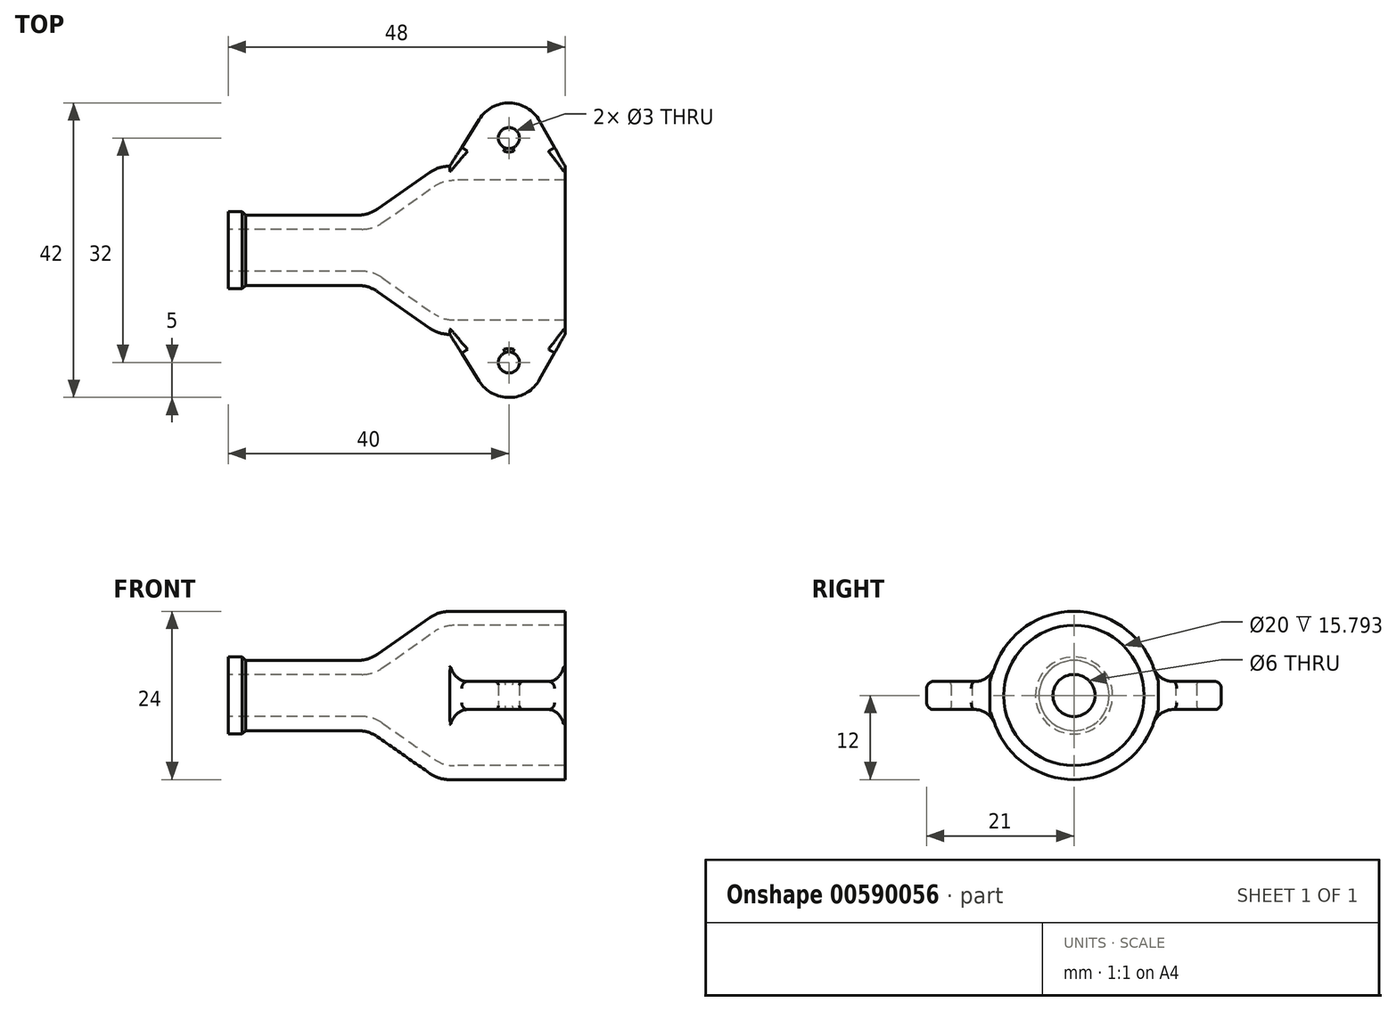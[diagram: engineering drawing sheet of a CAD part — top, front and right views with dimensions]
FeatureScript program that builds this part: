
annotation { "Feature Type Name" : "Feature", "Feature Type Description" : "" }
export const myFeature = defineFeature(function(context is Context, id is Id, definition is map)
    precondition{}
    {
        {
            var Q0;
            Q0=qCreatedBy(makeId("Front.planeOp"),FACE);
            var sketch = newSketch(context, id + "F0", { "sketchPlane" : qUnion([Q0])});
            skLineSegment(sketch, "E0", {"start": v(-50.98, 0) * mm, "end": v(49.02, 0) * mm, "construction": true});
            skLineSegment(sketch, "E1", {"start": v(-41.63, 5) * mm, "end": v(-23.63, 5) * mm});
            skLineSegment(sketch, "E2", {"start": v(-23.63, 5) * mm, "end": v(-13.63, 12) * mm});
            skLineSegment(sketch, "E3", {"start": v(-13.63, 12) * mm, "end": v(4.37, 12) * mm});
            skLineSegment(sketch, "E4", {"start": v(-43.63, 5) * mm, "end": v(-43.63, 3) * mm});
            skLineSegment(sketch, "E5", {"start": v(-43.63, 3) * mm, "end": v(-23, 3) * mm});
            skLineSegment(sketch, "E6", {"start": v(-23, 3) * mm, "end": v(-13, 10) * mm});
            skLineSegment(sketch, "E7", {"start": v(-13, 10) * mm, "end": v(4.37, 10) * mm});
            skLineSegment(sketch, "E8", {"start": v(4.37, 12) * mm, "end": v(4.37, 10) * mm});
            skLineSegment(sketch, "E9", {"start": v(-43.63, 5) * mm, "end": v(-43.63, 5.5) * mm});
            skLineSegment(sketch, "E10", {"start": v(-43.63, 5.5) * mm, "end": v(-41.63, 5.5) * mm});
            skLineSegment(sketch, "E11", {"start": v(-41.63, 5.5) * mm, "end": v(-41.63, 5) * mm});
            skSolve(sketch);
        }
        {
            var Q0;
            Q0 = qSketchRegion(id + "F0", true);
            var Q1;
            Q1=sQuery(id+"F0.wireOp",EDGE,"E0");
            revolve(context, id + "F1", {"entities" : qUnion([Q0]), "axis" : qUnion([Q1]), "revolveType" : RevolveType.FULL});
        }
        {
            var Q0;
            Q0=makeQuery(id+"F1.opRevolve","SWEPT_FACE",FACE,{"disambiguationData":[OSD([sQuery(id+"F0.wireOp",EDGE,"E8")])]});
            var sketch = newSketch(context, id + "F2", { "sketchPlane" : qUnion([Q0])});
            skLineSegment(sketch, "E12.bottom", {"start": v(-0.5, 25) * mm, "end": v(0.5, 25) * mm});
            skLineSegment(sketch, "E12.top", {"start": v(-0.5, -25) * mm, "end": v(0.5, -25) * mm});
            skLineSegment(sketch, "E12.left", {"start": v(-0.5, 25) * mm, "end": v(-0.5, 0.5) * mm});
            skLineSegment(sketch, "E12.right", {"start": v(0.5, 25) * mm, "end": v(0.5, 0.5) * mm});
            skLineSegment(sketch, "E13.bottom", {"start": v(-25, 0.5) * mm, "end": v(-0.5, 0.5) * mm});
            skLineSegment(sketch, "E13.top", {"start": v(-25, -0.5) * mm, "end": v(-0.5, -0.5) * mm});
            skLineSegment(sketch, "E13.left", {"start": v(-25, 0.5) * mm, "end": v(-25, -0.5) * mm});
            skLineSegment(sketch, "E13.right", {"start": v(25, 0.5) * mm, "end": v(25, -0.5) * mm});
            skLineSegment(sketch, "E14.trimOffspring", {"start": v(0.5, -0.5) * mm, "end": v(25, -0.5) * mm});
            skLineSegment(sketch, "E15.trimOffspring", {"start": v(0.5, 0.5) * mm, "end": v(25, 0.5) * mm});
            skLineSegment(sketch, "E16.trimOffspring", {"start": v(0.5, -0.5) * mm, "end": v(0.5, -25) * mm});
            skLineSegment(sketch, "E17.trimOffspring", {"start": v(-0.5, -0.5) * mm, "end": v(-0.5, -25) * mm});
            skSolve(sketch);
        }
        {
            var Q0;
            Q0=makeQuery(id+"F1.opRevolve","SWEPT_EDGE",EDGE,{"disambiguationData":[OSD([sQuery(id+"F0.wireOp",EDGE,"E1"),sQuery(id+"F0.wireOp",EDGE,"E2")])]});
            fillet(context, id + "F3", {"entities" : qUnion([Q0]), "radius" : 5 * mm, "tangentPropagation" : true, "allowEdgeOverflow" : false});
        }
        {
            var Q0;
            Q0=makeQuery(id+"F1.opRevolve","SWEPT_EDGE",EDGE,{"disambiguationData":[OSD([sQuery(id+"F0.wireOp",EDGE,"E2"),sQuery(id+"F0.wireOp",EDGE,"E3")])]});
            fillet(context, id + "F4", {"entities" : qUnion([Q0]), "radius" : 5 * mm, "tangentPropagation" : true, "allowEdgeOverflow" : false});
        }
        {
            var Q0;
            Q0=makeQuery(id+"F1.opRevolve","SWEPT_EDGE",EDGE,{"disambiguationData":[OSD([sQuery(id+"F0.wireOp",EDGE,"E6"),sQuery(id+"F0.wireOp",EDGE,"E7")])]});
            var Q1;
            Q1=makeQuery(id+"F1.opRevolve","SWEPT_EDGE",EDGE,{"disambiguationData":[OSD([sQuery(id+"F0.wireOp",EDGE,"E5"),sQuery(id+"F0.wireOp",EDGE,"E6")])]});
            fillet(context, id + "F5", {"entities" : qUnion([Q0, Q1]), "radius" : 5 * mm, "tangentPropagation" : true, "allowEdgeOverflow" : false});
        }
        {
            var Q0;
            Q0=makeQuery(id+"F1.opRevolve","SWEPT_EDGE",EDGE,{"disambiguationData":[OSD([sQuery(id+"F0.wireOp",EDGE,"E1"),sQuery(id+"F0.wireOp",EDGE,"E11")])]});
            chamfer(context, id + "F6", {"entities" : qUnion([Q0]), "width" : 0.5 * mm, "tangentPropagation" : true});
        }
        {
            var Q0;
            Q0=qCreatedBy(makeId("Top.planeOp"),FACE);
            var sketch = newSketch(context, id + "F7", { "sketchPlane" : qUnion([Q0])});
            skCircle(sketch, "E18", {"center": v(-3.63, 16) * mm, "radius": 1.5 * mm});
            skArc(sketch, "E19", {"start": v(0.72, 18.46) * mm, "mid": v(-3.51, 21) * mm, "end": v(-7.86, 18.66) * mm});
            skLineSegment(sketch, "E20", {"start": v(-12.05, 12) * mm, "end": v(-7.86, 18.66) * mm});
            skLineSegment(sketch, "E21", {"start": v(4.37, 12) * mm, "end": v(0.72, 18.46) * mm});
            skLineSegment(sketch, "E22", {"start": v(4.37, 12) * mm, "end": v(4.37, 10.56) * mm});
            skLineSegment(sketch, "E23", {"start": v(4.37, 10.56) * mm, "end": v(-12.05, 10.56) * mm});
            skLineSegment(sketch, "E24", {"start": v(-12.05, 10.56) * mm, "end": v(-12.05, 12) * mm});
            skSolve(sketch);
        }
        {
            var Q0;
            Q0 = qSketchRegion(id + "F7", true);
            extrude(context, id + "F8", {"entities" : qUnion([Q0]), "endBound" : BoundingType.SYMMETRIC, "depth" : 4 * mm, "offsetDistance" : 25 * mm});
        }
        {
            var Q0;
            Q0=makeQuery(id+"F8.opExtrude","SWEPT_BODY",BODY,{"disambiguationData":[OSD([sQuery(id+"F7.wireOp",EDGE,"E18"),sQuery(id+"F7.wireOp",EDGE,"E19"),sQuery(id+"F7.wireOp",EDGE,"E20"),sQuery(id+"F7.wireOp",EDGE,"E21"),sQuery(id+"F7.wireOp",EDGE,"E22"),sQuery(id+"F7.wireOp",EDGE,"E23"),sQuery(id+"F7.wireOp",EDGE,"E24")])]});
            var Q1;
            Q1=qCreatedBy(makeId("Front.planeOp"),FACE);
            mirror(context, id + "F9", {"entities" : qUnion([Q0]), "mirrorPlane" : qUnion([Q1])});
        }
        {
            var Q0;
            Q0=makeQuery(id+"F8.opExtrude","SWEPT_BODY",BODY,{"disambiguationData":[OSD([sQuery(id+"F7.wireOp",EDGE,"E18"),sQuery(id+"F7.wireOp",EDGE,"E19"),sQuery(id+"F7.wireOp",EDGE,"E20"),sQuery(id+"F7.wireOp",EDGE,"E21"),sQuery(id+"F7.wireOp",EDGE,"E22"),sQuery(id+"F7.wireOp",EDGE,"E23"),sQuery(id+"F7.wireOp",EDGE,"E24")])]});
            var Q1;
            Q1=makeQuery(id+"F1.opRevolve","SWEPT_BODY",BODY,{"disambiguationData":[OSD([sQuery(id+"F0.wireOp",EDGE,"E1"),sQuery(id+"F0.wireOp",EDGE,"E2"),sQuery(id+"F0.wireOp",EDGE,"E3"),sQuery(id+"F0.wireOp",EDGE,"E4"),sQuery(id+"F0.wireOp",EDGE,"E5"),sQuery(id+"F0.wireOp",EDGE,"E6"),sQuery(id+"F0.wireOp",EDGE,"E7"),sQuery(id+"F0.wireOp",EDGE,"E8"),sQuery(id+"F0.wireOp",EDGE,"E9"),sQuery(id+"F0.wireOp",EDGE,"E10"),sQuery(id+"F0.wireOp",EDGE,"E11")])]});
            var Q2;
            Q2=makeQuery(id+"F9.opPattern","COPY",BODY,{"derivedFrom":makeQuery(id+"F8.opExtrude","SWEPT_BODY",BODY,{"disambiguationData":[OSD([sQuery(id+"F7.wireOp",EDGE,"E18"),sQuery(id+"F7.wireOp",EDGE,"E19"),sQuery(id+"F7.wireOp",EDGE,"E20"),sQuery(id+"F7.wireOp",EDGE,"E21"),sQuery(id+"F7.wireOp",EDGE,"E22"),sQuery(id+"F7.wireOp",EDGE,"E23"),sQuery(id+"F7.wireOp",EDGE,"E24")])]}),"instanceName":"1"});
            booleanBodies(context, id + "F10", {"operationType" : BooleanOperationType.UNION, "tools" : qUnion([Q0, Q1, Q2])});
        }
        {
            var Q0;
            Q0=makeQuery(id+"F10.opBoolean","INTERSECT",EDGE,{"derivedFrom":[makeQuery(id+"F1.opRevolve","SWEPT_FACE",FACE,{"disambiguationData":[OSD([sQuery(id+"F0.wireOp",EDGE,"E3")])]}),makeQuery(id+"F9.opPattern","COPY",FACE,{"derivedFrom":makeQuery(id+"F8.opExtrude","CAP_FACE",FACE,{"disambiguationData":[OSD([sQuery(id+"F7.wireOp",EDGE,"E18"),sQuery(id+"F7.wireOp",EDGE,"E19"),sQuery(id+"F7.wireOp",EDGE,"E20"),sQuery(id+"F7.wireOp",EDGE,"E21"),sQuery(id+"F7.wireOp",EDGE,"E22"),sQuery(id+"F7.wireOp",EDGE,"E23"),sQuery(id+"F7.wireOp",EDGE,"E24")])],"isStart":false}),"instanceName":"1"})]});
            var Q1;
            Q1=makeQuery(id+"F10.opBoolean","INTERSECT",EDGE,{"derivedFrom":[makeQuery(id+"F1.opRevolve","SWEPT_FACE",FACE,{"disambiguationData":[OSD([sQuery(id+"F0.wireOp",EDGE,"E3")])]}),makeQuery(id+"F8.opExtrude","CAP_FACE",FACE,{"disambiguationData":[OSD([sQuery(id+"F7.wireOp",EDGE,"E18"),sQuery(id+"F7.wireOp",EDGE,"E19"),sQuery(id+"F7.wireOp",EDGE,"E20"),sQuery(id+"F7.wireOp",EDGE,"E21"),sQuery(id+"F7.wireOp",EDGE,"E22"),sQuery(id+"F7.wireOp",EDGE,"E23"),sQuery(id+"F7.wireOp",EDGE,"E24")])],"isStart":false})]});
            var Q2;
            Q2=makeQuery(id+"F10.opBoolean","INTERSECT",EDGE,{"derivedFrom":[makeQuery(id+"F1.opRevolve","SWEPT_FACE",FACE,{"disambiguationData":[OSD([sQuery(id+"F0.wireOp",EDGE,"E3")])]}),makeQuery(id+"F8.opExtrude","CAP_FACE",FACE,{"disambiguationData":[OSD([sQuery(id+"F7.wireOp",EDGE,"E18"),sQuery(id+"F7.wireOp",EDGE,"E19"),sQuery(id+"F7.wireOp",EDGE,"E20"),sQuery(id+"F7.wireOp",EDGE,"E21"),sQuery(id+"F7.wireOp",EDGE,"E22"),sQuery(id+"F7.wireOp",EDGE,"E23"),sQuery(id+"F7.wireOp",EDGE,"E24")])],"isStart":true})]});
            var Q3;
            Q3=makeQuery(id+"F10.opBoolean","INTERSECT",EDGE,{"derivedFrom":[makeQuery(id+"F1.opRevolve","SWEPT_FACE",FACE,{"disambiguationData":[OSD([sQuery(id+"F0.wireOp",EDGE,"E3")])]}),makeQuery(id+"F9.opPattern","COPY",FACE,{"derivedFrom":makeQuery(id+"F8.opExtrude","CAP_FACE",FACE,{"disambiguationData":[OSD([sQuery(id+"F7.wireOp",EDGE,"E18"),sQuery(id+"F7.wireOp",EDGE,"E19"),sQuery(id+"F7.wireOp",EDGE,"E20"),sQuery(id+"F7.wireOp",EDGE,"E21"),sQuery(id+"F7.wireOp",EDGE,"E22"),sQuery(id+"F7.wireOp",EDGE,"E23"),sQuery(id+"F7.wireOp",EDGE,"E24")])],"isStart":true}),"instanceName":"1"})]});
            fillet(context, id + "F11", {"entities" : qUnion([Q0, Q1, Q2, Q3]), "radius" : 3 * mm, "tangentPropagation" : true, "allowEdgeOverflow" : false});
        }
        {
            var Q0;
            Q0=makeQuery(id+"F9.opPattern","COPY",EDGE,{"derivedFrom":makeQuery(id+"F8.opExtrude","CAP_EDGE",EDGE,{"disambiguationData":[OSD([sQuery(id+"F7.wireOp",EDGE,"E20")])],"isStart":true}),"instanceName":"1"});
            var Q1;
            Q1=makeQuery(id+"F9.opPattern","COPY",EDGE,{"derivedFrom":makeQuery(id+"F8.opExtrude","CAP_EDGE",EDGE,{"disambiguationData":[OSD([sQuery(id+"F7.wireOp",EDGE,"E19")])],"isStart":false}),"instanceName":"1"});
            var Q2;
            Q2=makeQuery(id+"F8.opExtrude","CAP_EDGE",EDGE,{"disambiguationData":[OSD([sQuery(id+"F7.wireOp",EDGE,"E20")])],"isStart":true});
            var Q3;
            Q3=makeQuery(id+"F8.opExtrude","CAP_EDGE",EDGE,{"disambiguationData":[OSD([sQuery(id+"F7.wireOp",EDGE,"E20")])],"isStart":false});
            fillet(context, id + "F12", {"entities" : qUnion([Q0, Q1, Q2, Q3]), "radius" : 1 * mm, "tangentPropagation" : true, "allowEdgeOverflow" : false});
        }
        {
            var Q0;
            Q0=makeQuery(id+"F8.opExtrude","CAP_EDGE",EDGE,{"disambiguationData":[OSD([sQuery(id+"F7.wireOp",EDGE,"E18")])],"isStart":true});
            var Q1;
            Q1=makeQuery(id+"F9.opPattern","COPY",EDGE,{"derivedFrom":makeQuery(id+"F8.opExtrude","CAP_EDGE",EDGE,{"disambiguationData":[OSD([sQuery(id+"F7.wireOp",EDGE,"E18")])],"isStart":true}),"instanceName":"1"});
            var Q2;
            Q2=makeQuery(id+"F8.opExtrude","CAP_EDGE",EDGE,{"disambiguationData":[OSD([sQuery(id+"F7.wireOp",EDGE,"E18")])],"isStart":false});
            var Q3;
            Q3=makeQuery(id+"F9.opPattern","COPY",EDGE,{"derivedFrom":makeQuery(id+"F8.opExtrude","CAP_EDGE",EDGE,{"disambiguationData":[OSD([sQuery(id+"F7.wireOp",EDGE,"E18")])],"isStart":false}),"instanceName":"1"});
            fillet(context, id + "F13", {"entities" : qUnion([Q0, Q1, Q2, Q3]), "radius" : 0.5 * mm, "tangentPropagation" : true, "allowEdgeOverflow" : false});
        }
    });
